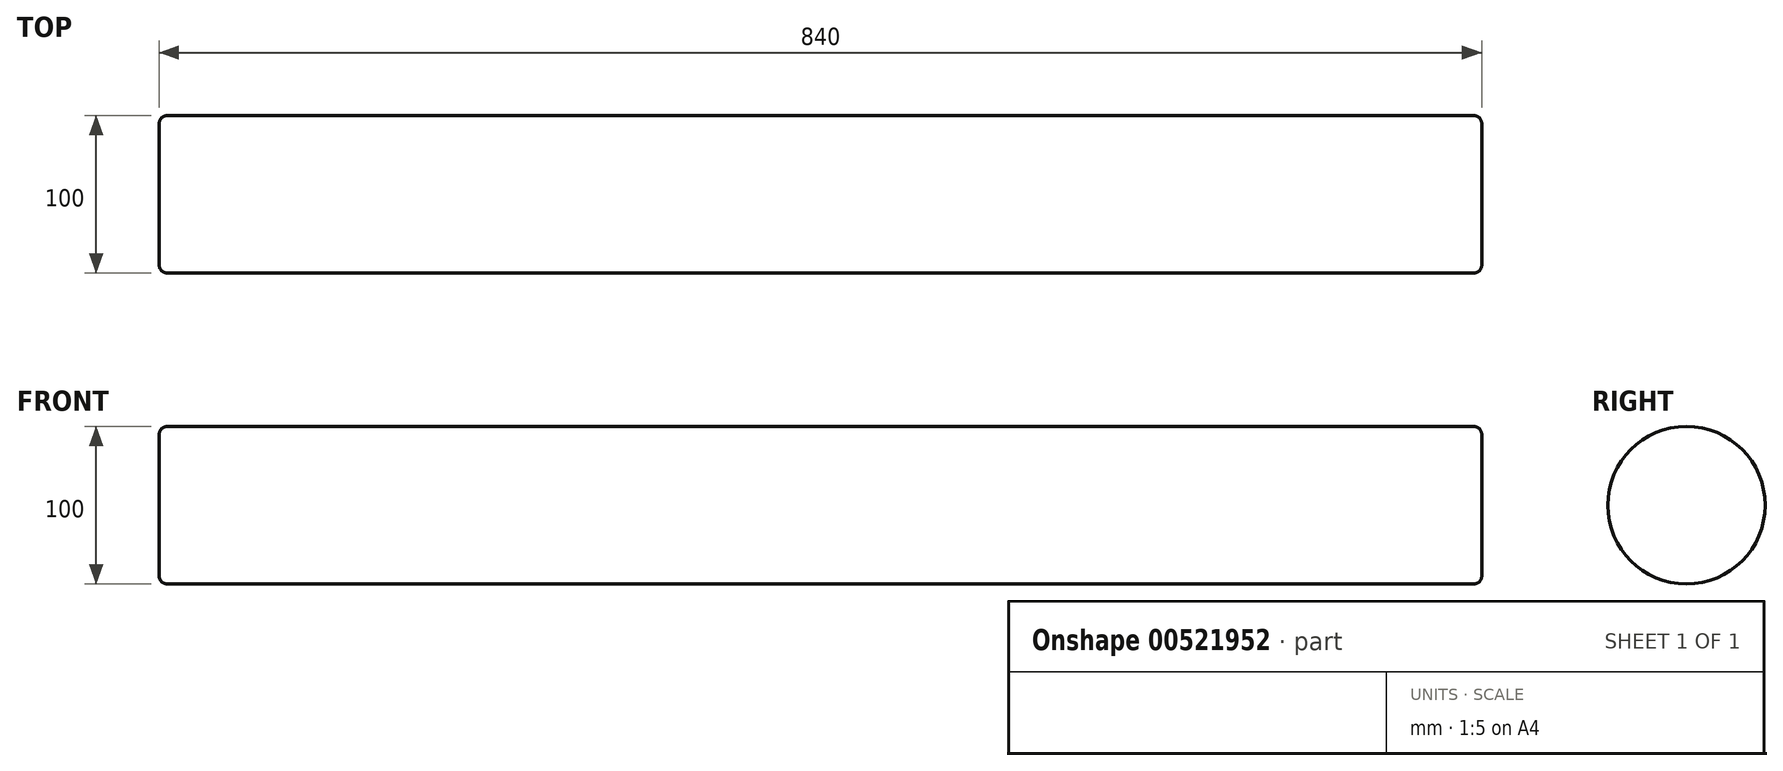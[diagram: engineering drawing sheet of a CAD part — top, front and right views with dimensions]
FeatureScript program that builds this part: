
annotation { "Feature Type Name" : "Feature", "Feature Type Description" : "" }
export const myFeature = defineFeature(function(context is Context, id is Id, definition is map)
    precondition{}
    {
        {
            var Q0;
            Q0=qCreatedBy(makeId("Right.planeOp"),FACE);
            var sketch = newSketch(context, id + "F0", { "sketchPlane" : qUnion([Q0])});
            skCircle(sketch, "E0", {"center": v(0, 0) * mm, "radius": 50 * mm});
            skSolve(sketch);
        }
        {
            var Q0;
            Q0=makeQuery(id+"F0.imprint","IMPRINT",FACE,{"disambiguationData":[TD([[makeQuery(id+"F0.imprint","IMPRINT",EDGE,{"derivedFrom":sQuery(id+"F0.wireOp",EDGE,"E0")}),1.0]])]});
            var Q1;
            Q1=sQuery(id+"F0.wireOp",EDGE,"E0");
            extrude(context, id + "F1", {"entities" : qUnion([Q0]), "surfaceEntities" : qUnion([Q1]), "depth" : 420 * mm, "offsetDistance" : 25 * mm, "hasSecondDirection" : true, "secondDirectionOppositeDirection" : true, "secondDirectionDepth" : 420 * mm});
        }
        {
            var Q0;
            Q0=makeQuery(id+"F1.opExtrude","CAP_EDGE",EDGE,{"disambiguationData":[OSD([sQuery(id+"F0.wireOp",EDGE,"E0")])],"isStart":false});
            var Q1;
            Q1=makeQuery(id+"F1.opExtrude","CAP_EDGE",EDGE,{"disambiguationData":[OSD([sQuery(id+"F0.wireOp",EDGE,"E0")])],"isStart":true});
            fillet(context, id + "F2", {"entities" : qUnion([Q0, Q1]), "radius" : 5 * mm, "tangentPropagation" : true, "allowEdgeOverflow" : false});
        }
    });
